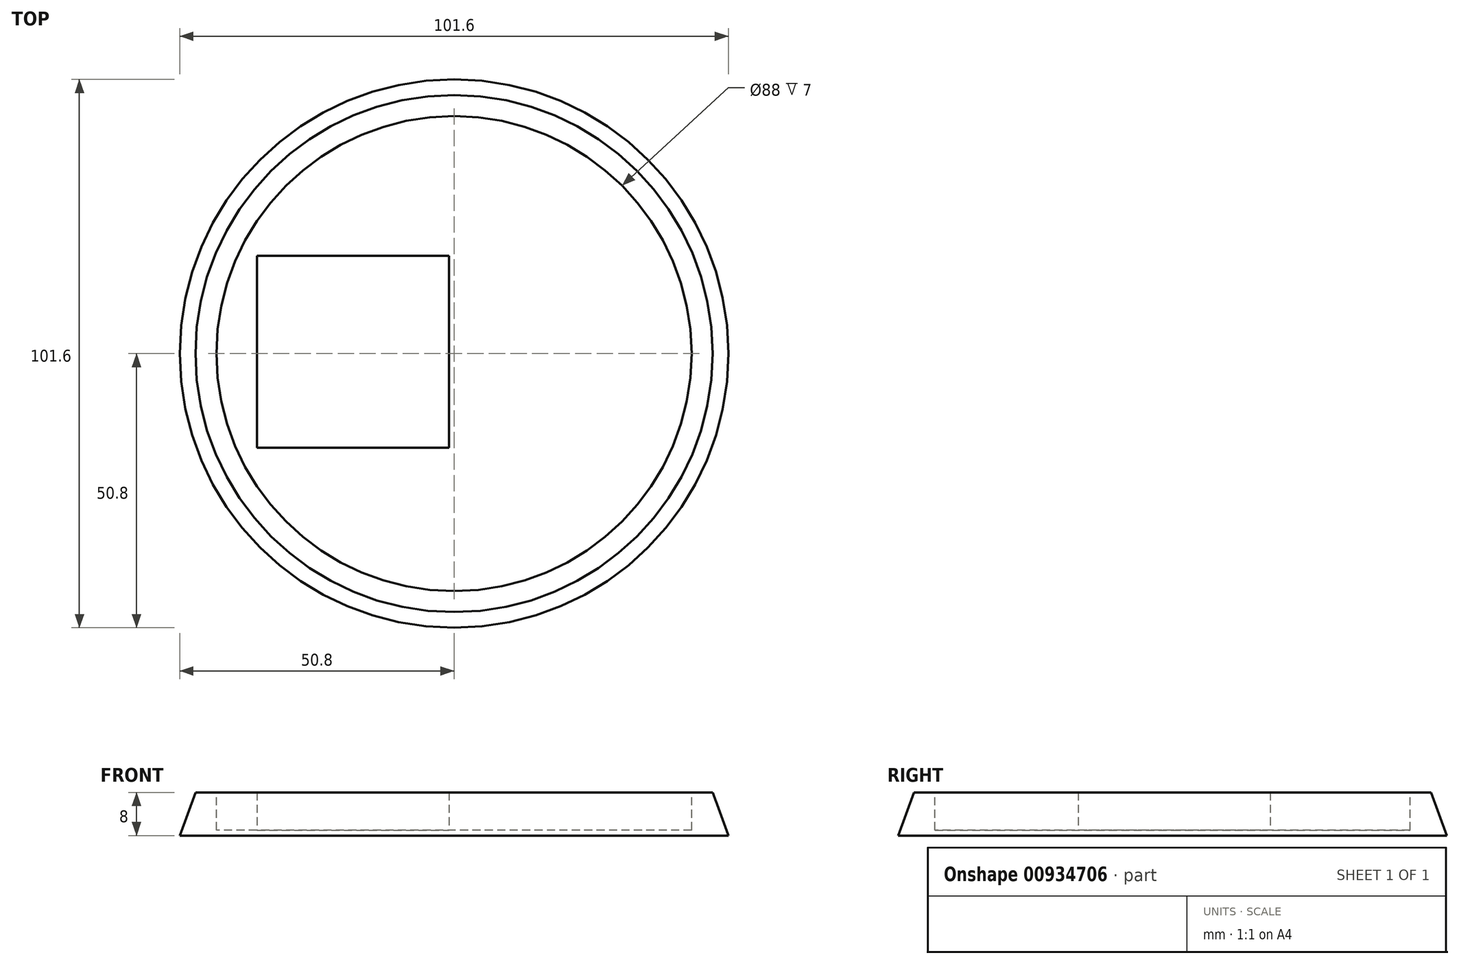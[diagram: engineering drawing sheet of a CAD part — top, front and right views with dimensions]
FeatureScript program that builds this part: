
annotation { "Feature Type Name" : "Feature", "Feature Type Description" : "" }
export const myFeature = defineFeature(function(context is Context, id is Id, definition is map)
    precondition{}
    {
        {
            var Q0;
            Q0=qCreatedBy(makeId("Top.planeOp"),FACE);
            var sketch = newSketch(context, id + "F0", { "sketchPlane" : qUnion([Q0])});
            skCircle(sketch, "E0", {"center": v(0, 0) * mm, "radius": 50.8 * mm});
            skSolve(sketch);
        }
        {
            var Q0;
            Q0=makeQuery(id+"F0.imprint","IMPRINT",FACE,{"disambiguationData":[TD([[makeQuery(id+"F0.imprint","IMPRINT",EDGE,{"derivedFrom":sQuery(id+"F0.wireOp",EDGE,"E0")}),1.0]])]});
            extrude(context, id + "F1", {"entities" : qUnion([Q0]), "depth" : 8 * mm, "offsetDistance" : 25.4 * mm, "hasDraft" : true, "draftAngle" : 20 * degree, "draftPullDirection" : true});
        }
        {
            var Q0;
            Q0=makeQuery(id+"F1.opExtrude","CAP_FACE",FACE,{"disambiguationData":[OSD([sQuery(id+"F0.wireOp",EDGE,"E0")])],"isStart":false});
            var sketch = newSketch(context, id + "F2", { "sketchPlane" : qUnion([Q0])});
            skCircle(sketch, "E1", {"center": v(0, 0) * mm, "radius": 44 * mm});
            skSolve(sketch);
        }
        {
            var Q0;
            Q0 = qSketchRegion(id + "F2", true);
            extrude(context, id + "F3", {"entities" : qUnion([Q0]), "operationType" : NewBodyOperationType.REMOVE, "oppositeDirection" : true, "depth" : 7 * mm, "offsetDistance" : 25.4 * mm});
        }
        {
            var Q0;
            Q0=makeQuery(id+"F3.boolean.opBoolean","COPY",FACE,{"derivedFrom":makeQuery(id+"F3.opExtrude","CAP_FACE",FACE,{"disambiguationData":[OSD([sQuery(id+"F2.wireOp",EDGE,"E1")])],"isStart":false})});
            var sketch = newSketch(context, id + "F4", { "sketchPlane" : qUnion([Q0])});
            skLineSegment(sketch, "E2.bottom", {"start": v(-36.49, 18.1) * mm, "end": v(-0.93, 18.1) * mm});
            skLineSegment(sketch, "E2.top", {"start": v(-36.49, -17.45) * mm, "end": v(-0.93, -17.45) * mm});
            skLineSegment(sketch, "E2.left", {"start": v(-36.49, 18.1) * mm, "end": v(-36.49, -17.45) * mm});
            skLineSegment(sketch, "E2.right", {"start": v(-0.93, 18.1) * mm, "end": v(-0.93, -17.45) * mm});
            skSolve(sketch);
        }
        {
            var Q0;
            Q0 = qSketchRegion(id + "F4", true);
            extrude(context, id + "F5", {"entities" : qUnion([Q0]), "depth" : 7 * mm, "offsetDistance" : 25.4 * mm});
        }
        {
            var Q0;
            Q0=qCreatedBy(makeId("Right.planeOp"),FACE);
            cPlane(context, id + "F6", {"entities" : qUnion([Q0]), "cplaneType" : CPlaneType.OFFSET, "offset" : 40 * mm, "width" : 152.4 * mm, "height" : 152.4 * mm});
        }
        {
            var Q0;
            Q0=qCreatedBy(id+"F6.planeOp",FACE);
            var sketch = newSketch(context, id + "F7", { "sketchPlane" : qUnion([Q0])});
            skCircle(sketch, "E3", {"center": v(0, 5.61) * mm, "radius": 2.16 * mm});
            skSolve(sketch);
        }
        {
            var Q0;
            Q0 = qSketchRegion(id + "F7", true);
            extrude(context, id + "F8", {"entities" : qUnion([Q0]), "operationType" : NewBodyOperationType.REMOVE, "oppositeDirection" : true, "depth" : 25.4 * mm, "offsetDistance" : 25.4 * mm});
        }
    });
